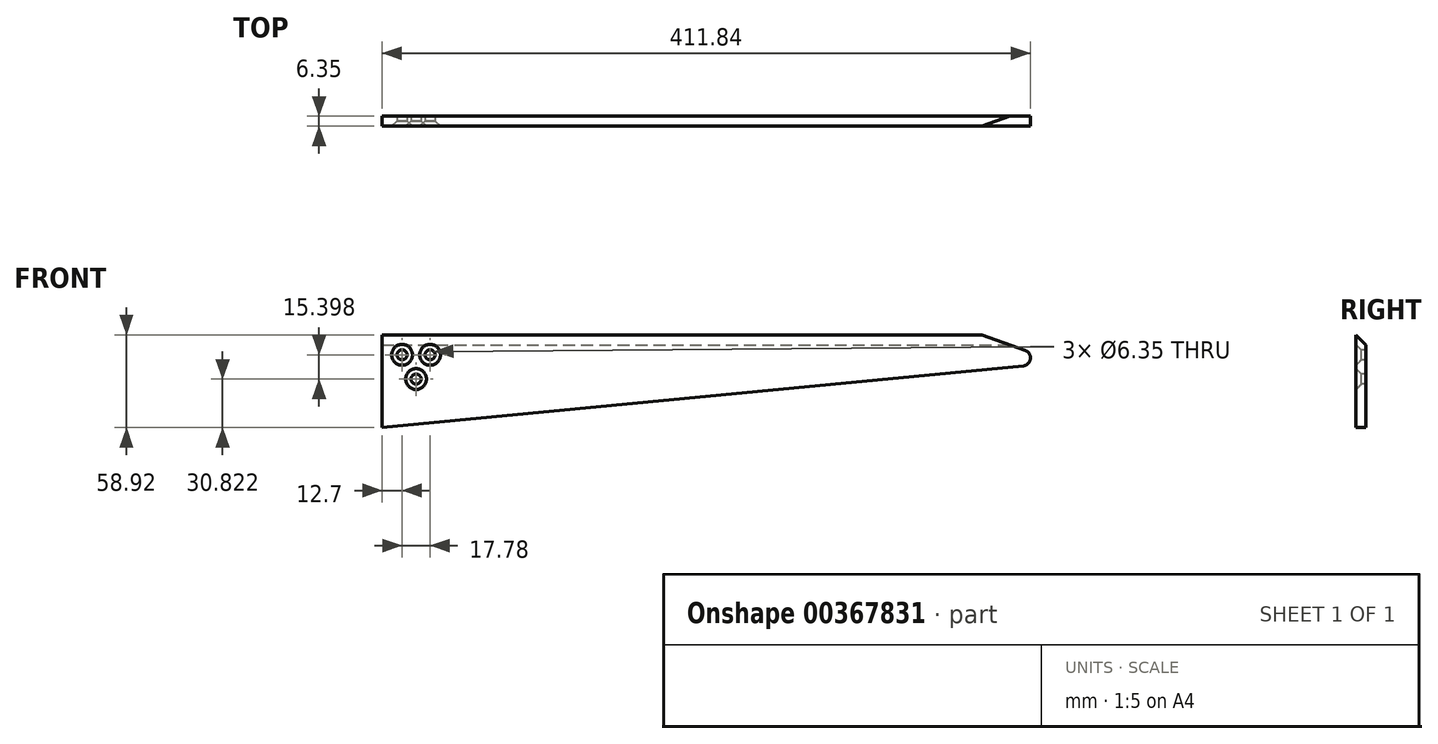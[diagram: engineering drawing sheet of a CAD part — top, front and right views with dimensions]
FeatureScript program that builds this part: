
annotation { "Feature Type Name" : "Feature", "Feature Type Description" : "" }
export const myFeature = defineFeature(function(context is Context, id is Id, definition is map)
    precondition{}
    {
        {
            var Q0;
            Q0=qCreatedBy(makeId("Front.planeOp"),FACE);
            var sketch = newSketch(context, id + "F0", { "sketchPlane" : qUnion([Q0])});
            skLineSegment(sketch, "E0", {"start": v(0, 0) * mm, "end": v(381, 0) * mm});
            skLineSegment(sketch, "E1", {"start": v(0, 0) * mm, "end": v(0, -58.92) * mm});
            skLineSegment(sketch, "E2", {"start": v(0, -58.92) * mm, "end": v(407.24, -19.7) * mm});
            skLineSegment(sketch, "E3", {"start": v(408.47, -9.87) * mm, "end": v(381, 0) * mm});
            skPoint(sketch, "E4.visualSharp", {"position": v(429.81, -17.53) * mm});
            skArc(sketch, "E4.filletArc", {"start": v(407.24, -19.7) * mm, "mid": v(411.8, -15.28) * mm, "end": v(408.47, -9.87) * mm});
            skSolve(sketch);
        }
        {
            var Q0;
            Q0 = qSketchRegion(id + "F0", true);
            extrude(context, id + "F1", {"entities" : qUnion([Q0]), "depth" : 6.35 * mm});
        }
        {
            var Q0;
            Q0=makeQuery(id+"F1.opExtrude","CAP_FACE",FACE,{"disambiguationData":[OSD([sQuery(id+"F0.wireOp",EDGE,"E0"),sQuery(id+"F0.wireOp",EDGE,"E1"),sQuery(id+"F0.wireOp",EDGE,"E2"),sQuery(id+"F0.wireOp",EDGE,"E3")])],"isStart":false});
            var sketch = newSketch(context, id + "F2", { "sketchPlane" : qUnion([Q0])});
            skCircle(sketch, "E5", {"center": v(12.7, -12.7) * mm, "radius": 4.58 * mm});
            skCircle(sketch, "E6", {"center": v(30.48, -12.7) * mm, "radius": 5.13 * mm});
            skCircle(sketch, "E7", {"center": v(21.6, -28.1) * mm, "radius": 4.31 * mm});
            skSolve(sketch);
        }
        {
            var Q0;
            Q0=sQuery(id+"F2.wireOp",VERTEX,"E5.center");
            var Q1;
            Q1=sQuery(id+"F2.wireOp",VERTEX,"E6.center");
            var Q2;
            Q2=sQuery(id+"F2.wireOp",VERTEX,"E7.center");
            var Q3;
            Q3=makeQuery(id+"F1.opExtrude","SWEPT_BODY",BODY,{"disambiguationData":[OSD([sQuery(id+"F0.wireOp",EDGE,"E0"),sQuery(id+"F0.wireOp",EDGE,"E1"),sQuery(id+"F0.wireOp",EDGE,"E2"),sQuery(id+"F0.wireOp",EDGE,"E3")])]});
            hole(context, id + "F3", {"style" : HoleStyle.C_SINK, "endStyle" : HoleEndStyle.THROUGH, "holeDiameter" : 6.35 * mm, "cSinkDiameter" : 13.2 * mm, "cSinkAngle" : 90 * degree, "isTappedThrough" : true, "tappedDepth" : 12.7 * mm, "tapClearance" : 3, "locations" : qUnion([Q0, Q1, Q2]), "scope" : qUnion([Q3])});
        }
        {
            var Q0;
            Q0=makeQuery(id+"F1.opExtrude","CAP_EDGE",EDGE,{"disambiguationData":[OSD([sQuery(id+"F0.wireOp",EDGE,"E0")])],"isStart":true});
            chamfer(context, id + "F4", {"entities" : qUnion([Q0]), "width" : 6.35 * mm, "tangentPropagation" : true});
        }
    });
